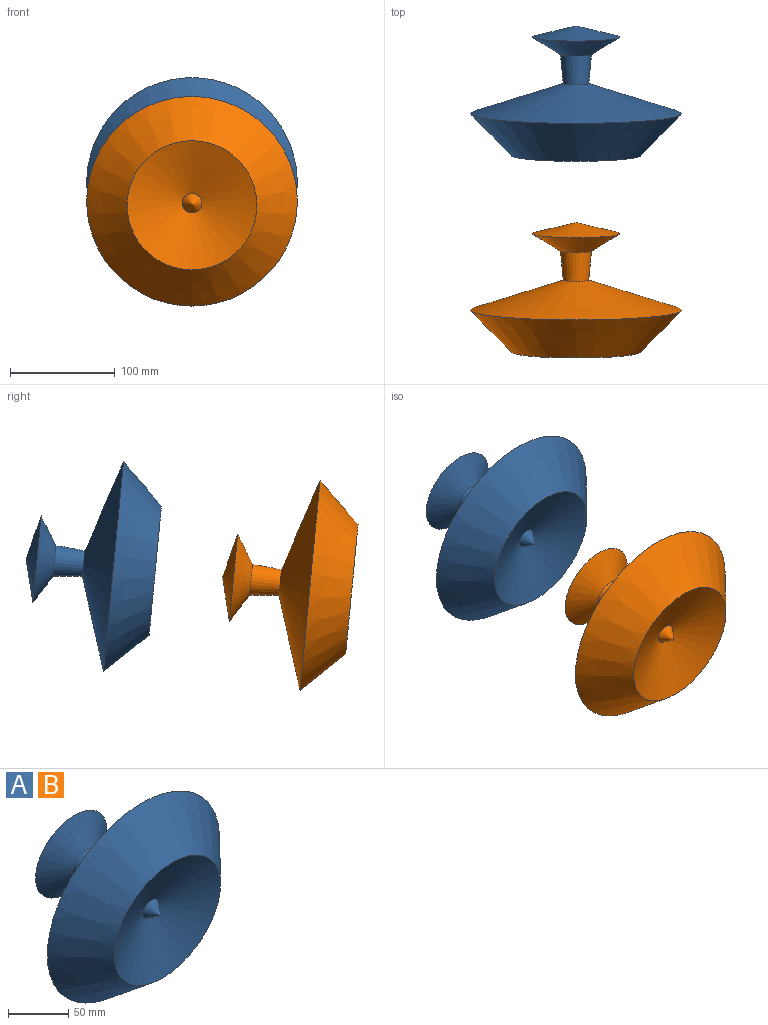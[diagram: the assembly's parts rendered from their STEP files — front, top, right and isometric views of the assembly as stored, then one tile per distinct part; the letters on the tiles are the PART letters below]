
ASSEMBLY  parts=2 mates=1
PART A: 7 faces, bbox 200.6x129x199.7 mm
  f0: cone r=9.27mm half-angle=39.1deg, axis (0,1,0.1), area 428.5mm2, adj f1
  f1: cone r=61.82mm half-angle=69.4deg, axis (0,-1,-0.1), area 12541.3mm2, adj f0,f2
  f2: cone r=100.31mm half-angle=43.9deg, axis (0,1,0.1), area 28269.2mm2, adj f1,f3
  f3: cone r=12.18mm half-angle=72deg, axis (0,-1,-0.1), area 32744.4mm2, adj f2,f4
  f4: cone r=14.85mm half-angle=5.5deg, axis (0,1,0.1), area 2379.6mm2, adj f3,f5
  f5: cone r=41.53mm half-angle=57.9deg, axis (0,1,0.1), area 5578.8mm2, adj f4,f6
  f6: cone r=0mm half-angle=75.8deg, axis (0,-1,-0.1), area 5589.5mm2, adj f5
PART B: same geometry as A
PLACE A t=(-4.87,67.72,39.16)mm
PLACE B t=(-4.87,-119.48,21.29)mm
MATE slider B.f6 <-> A.f6  axis (0,-1,-0.1) through (-4.87,-70.37,72.44)mm
